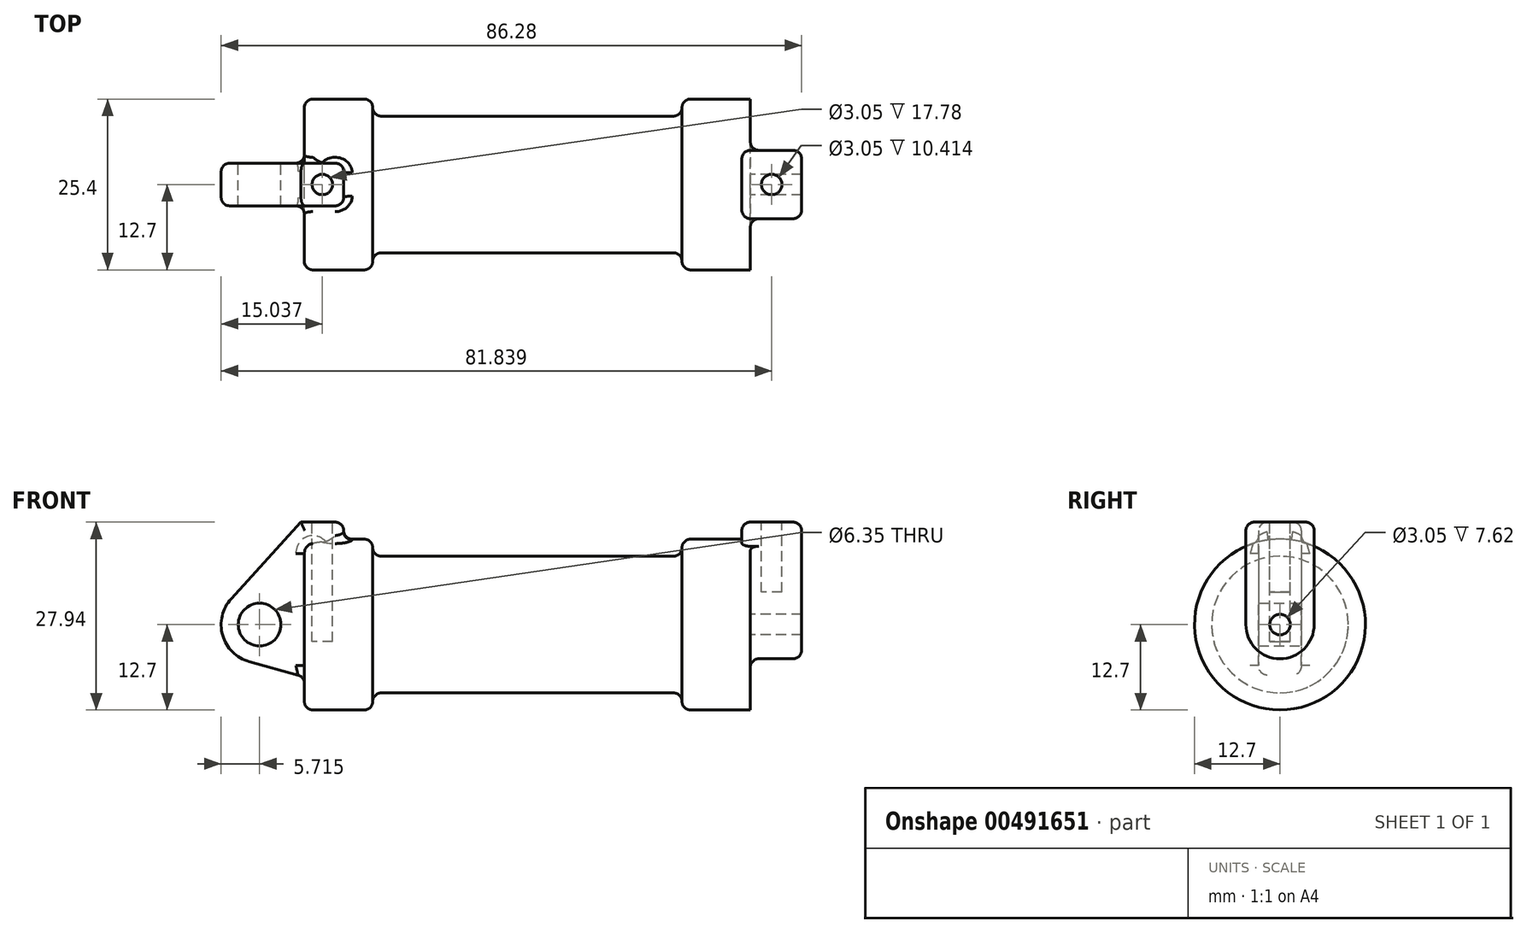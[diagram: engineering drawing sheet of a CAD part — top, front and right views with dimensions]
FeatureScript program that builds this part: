
annotation { "Feature Type Name" : "Feature", "Feature Type Description" : "" }
export const myFeature = defineFeature(function(context is Context, id is Id, definition is map)
    precondition{}
    {
        {
            var Q0;
            Q0=qCreatedBy(makeId("Front.planeOp"),FACE);
            var sketch = newSketch(context, id + "F0", { "sketchPlane" : qUnion([Q0])});
            skLineSegment(sketch, "E0", {"start": v(0, 0) * mm, "end": v(0, 12.7) * mm});
            skLineSegment(sketch, "E1", {"start": v(0, 12.7) * mm, "end": v(10.16, 12.7) * mm});
            skLineSegment(sketch, "E2", {"start": v(10.16, 12.7) * mm, "end": v(10.16, 10.16) * mm});
            skLineSegment(sketch, "E3", {"start": v(10.16, 10.16) * mm, "end": v(56.13, 10.16) * mm});
            skLineSegment(sketch, "E4", {"start": v(56.13, 10.16) * mm, "end": v(56.13, 12.7) * mm});
            skLineSegment(sketch, "E5", {"start": v(56.13, 12.7) * mm, "end": v(66.3, 12.7) * mm});
            skLineSegment(sketch, "E6", {"start": v(66.3, 12.7) * mm, "end": v(66.3, 0) * mm});
            skLineSegment(sketch, "E7", {"start": v(66.3, 0) * mm, "end": v(0, 0) * mm});
            skLineSegment(sketch, "E8", {"start": v(5.84, 15.24) * mm, "end": v(-0.5, 15.24) * mm});
            skLineSegment(sketch, "E9", {"start": v(-0.5, 15.24) * mm, "end": v(-10.88, 3.85) * mm});
            skLineSegment(sketch, "E10", {"start": v(0, 0) * mm, "end": v(-6.65, 0) * mm});
            skCircle(sketch, "E11", {"center": v(-6.65, 0) * mm, "radius": 5.72 * mm});
            skCircle(sketch, "E12", {"center": v(-6.65, 0) * mm, "radius": 3.18 * mm});
            skLineSegment(sketch, "E13", {"start": v(5.84, 15.24) * mm, "end": v(5.84, -9.4) * mm});
            skLineSegment(sketch, "E14", {"start": v(5.84, -9.4) * mm, "end": v(-8.18, -5.5) * mm});
            skSolve(sketch);
        }
        {
            var Q0;
            {var subQ0=sQuery(id+"F0.wireOp",EDGE,"E0");Q0=makeQuery(id+"F0.imprint","IMPRINT",FACE,{"disambiguationData":[TD([[makeQuery(id+"F0.imprint","IMPRINT",EDGE,{"derivedFrom":subQ0}),-1.0]])]});}
            var Q1;
            {var subQ0=sQuery(id+"F0.wireOp",EDGE,"E2");Q1=makeQuery(id+"F0.imprint","IMPRINT",FACE,{"disambiguationData":[TD([[makeQuery(id+"F0.imprint","IMPRINT",EDGE,{"derivedFrom":subQ0}),-1.0]])]});}
            var Q2;
            Q2=sQuery(id+"F0.wireOp",EDGE,"E7");
            revolve(context, id + "F1", {"entities" : qUnion([Q0, Q1]), "axis" : qUnion([Q2]), "revolveType" : RevolveType.FULL});
        }
        {
            var Q0;
            {var subQ5=sQuery(id+"F0.wireOp",EDGE,"E12");Q0=makeQuery(id+"F0.imprint","IMPRINT",FACE,{"disambiguationData":[TD([[makeQuery(id+"F0.imprint","IMPRINT",EDGE,{"derivedFrom":subQ5}),-1.0]])]});}
            var Q1;
            {var subQ1=sQuery(id+"F0.wireOp",EDGE,"E0");Q1=makeQuery(id+"F0.imprint","IMPRINT",FACE,{"disambiguationData":[TD([[makeQuery(id+"F0.imprint","IMPRINT",EDGE,{"derivedFrom":subQ1}),1.0]])]});}
            var Q2;
            {var subQ0=sQuery(id+"F0.wireOp",EDGE,"E0");Q2=makeQuery(id+"F0.imprint","IMPRINT",FACE,{"disambiguationData":[TD([[makeQuery(id+"F0.imprint","IMPRINT",EDGE,{"derivedFrom":subQ0}),-1.0]])]});}
            var Q3;
            {var subQ0=sQuery(id+"F0.wireOp",EDGE,"E14");Q3=makeQuery(id+"F0.imprint","IMPRINT",FACE,{"disambiguationData":[TD([[makeQuery(id+"F0.imprint","IMPRINT",EDGE,{"derivedFrom":subQ0}),-1.0]])]});}
            extrude(context, id + "F2", {"entities" : qUnion([Q0, Q1, Q2, Q3]), "operationType" : NewBodyOperationType.ADD, "endBound" : BoundingType.SYMMETRIC, "depth" : 6.35 * mm});
        }
        {
            var Q0;
            Q0=makeQuery(id+"F1.opRevolve","SWEPT_FACE",FACE,{"disambiguationData":[OSD([sQuery(id+"F0.wireOp",EDGE,"E6")])]});
            var sketch = newSketch(context, id + "F3", { "sketchPlane" : qUnion([Q0])});
            skCircle(sketch, "E15", {"center": v(0, 0) * mm, "radius": 5.08 * mm});
            skCircle(sketch, "E16", {"center": v(0, 0) * mm, "radius": 1.52 * mm});
            skLineSegment(sketch, "E17", {"start": v(-5.08, 15.24) * mm, "end": v(5.08, 15.24) * mm});
            skLineSegment(sketch, "E18", {"start": v(-5.08, 15.24) * mm, "end": v(-5.08, 0) * mm});
            skLineSegment(sketch, "E19", {"start": v(5.08, 15.24) * mm, "end": v(5.08, 0) * mm});
            skSolve(sketch);
        }
        {
            var Q0;
            {var subQ0=sQuery(id+"F3.wireOp",EDGE,"E17");Q0=makeQuery(id+"F3.imprint","IMPRINT",FACE,{"disambiguationData":[TD([[makeQuery(id+"F3.imprint","IMPRINT",EDGE,{"derivedFrom":subQ0}),-1.0]])]});}
            var Q1;
            {var subQ0=sQuery(id+"F3.wireOp",EDGE,"E18");var subQ1=sQuery(id+"F3.wireOp",EDGE,"E15");var subQ2=makeQuery(id+"F3.imprint","INTERSECT",VERTEX,{"derivedFrom":[subQ1,subQ0]});Q1=makeQuery(id+"F3.imprint","IMPRINT",FACE,{"disambiguationData":[TD([[makeQuery(id+"F3.imprint","IMPRINT",EDGE,{"disambiguationData":[TD([[subQ2,1.0]])],"derivedFrom":subQ1}),-1.0]])]});}
            var Q2;
            Q2=makeQuery(id+"F3.imprint","IMPRINT",FACE,{"disambiguationData":[TD([[makeQuery(id+"F3.imprint","IMPRINT",EDGE,{"derivedFrom":sQuery(id+"F3.wireOp",EDGE,"E16")}),-1.0]])]});
            extrude(context, id + "F4", {"entities" : qUnion([Q0, Q1, Q2]), "operationType" : NewBodyOperationType.ADD, "depth" : 7.62 * mm});
        }
        {
            var Q0;
            Q0=makeQuery(id+"F4.opExtrude","CAP_FACE",FACE,{"disambiguationData":[OSD([sQuery(id+"F3.wireOp",EDGE,"E15"),sQuery(id+"F3.wireOp",EDGE,"E16"),sQuery(id+"F3.wireOp",EDGE,"E17"),sQuery(id+"F3.wireOp",EDGE,"E18"),sQuery(id+"F3.wireOp",EDGE,"E19")])],"isStart":true});
            extrude(context, id + "F5", {"entities" : qUnion([Q0]), "operationType" : NewBodyOperationType.ADD, "depth" : 1.27 * mm});
        }
        {
            var Q0;
            Q0=makeQuery(id+"F4.boolean.opBoolean","SPLIT",FACE,{"disambiguationData":[TD([makeQuery(id+"F4.opExtrude","SWEPT_FACE",FACE,{"disambiguationData":[OSD([sQuery(id+"F3.wireOp",EDGE,"E16")])]})])],"derivedFrom":makeQuery(id+"F1.opRevolve","SWEPT_FACE",FACE,{"disambiguationData":[OSD([sQuery(id+"F0.wireOp",EDGE,"E6")])]})});
            var Q1;
            Q1=makeQuery(id+"F1.opRevolve","SWEPT_FACE",FACE,{"disambiguationData":[OSD([sQuery(id+"F0.wireOp",EDGE,"E2")])]});
            extrude(context, id + "F6", {"entities" : qUnion([Q0]), "operationType" : NewBodyOperationType.ADD, "endBound" : BoundingType.UP_TO_SURFACE, "oppositeDirection" : true, "endBoundEntityFace" : qUnion([Q1]), "depth" : 25.4 * mm});
        }
        {
            var Q0;
            Q0=makeQuery(id+"F2.opExtrude","SWEPT_FACE",FACE,{"disambiguationData":[OSD([sQuery(id+"F0.wireOp",EDGE,"E8")])]});
            var sketch = newSketch(context, id + "F7", { "sketchPlane" : qUnion([Q0])});
            skLineSegment(sketch, "E20", {"start": v(2.67, 3.18) * mm, "end": v(2.67, -3.18) * mm, "construction": true});
            skCircle(sketch, "E21", {"center": v(2.67, 0) * mm, "radius": 1.52 * mm});
            skSolve(sketch);
        }
        {
            var Q0;
            {var subQ0=sQuery(id+"F3.wireOp",EDGE,"E17");Q0=makeQuery(id+"F5.boolean.opBoolean","MERGE",FACE,{"derivedFrom":[makeQuery(id+"F4.opExtrude","SWEPT_FACE",FACE,{"disambiguationData":[OSD([subQ0])]}),makeQuery(id+"F5.opExtrude","SWEPT_FACE",FACE,{"disambiguationData":[OSD([subQ0])]})]});}
            var sketch = newSketch(context, id + "F8", { "sketchPlane" : qUnion([Q0])});
            skLineSegment(sketch, "E22", {"start": v(65.02, 0) * mm, "end": v(73.91, 0) * mm, "construction": true});
            skCircle(sketch, "E23", {"center": v(69.47, 0) * mm, "radius": 1.52 * mm});
            skSolve(sketch);
        }
        {
            var Q0;
            Q0=makeQuery(id+"F7.imprint","IMPRINT",FACE,{"disambiguationData":[TD([[makeQuery(id+"F7.imprint","IMPRINT",EDGE,{"derivedFrom":sQuery(id+"F7.wireOp",EDGE,"E21")}),1.0]])]});
            extrude(context, id + "F9", {"entities" : qUnion([Q0]), "operationType" : NewBodyOperationType.REMOVE, "oppositeDirection" : true, "depth" : 17.78 * mm});
        }
        {
            var Q0;
            Q0=makeQuery(id+"F8.imprint","IMPRINT",FACE,{"disambiguationData":[TD([[makeQuery(id+"F8.imprint","IMPRINT",EDGE,{"derivedFrom":sQuery(id+"F8.wireOp",EDGE,"E23")}),1.0]])]});
            extrude(context, id + "F10", {"entities" : qUnion([Q0]), "operationType" : NewBodyOperationType.REMOVE, "oppositeDirection" : true, "depth" : 10.4 * mm});
        }
        {
            var Q0;
            Q0=makeQuery(id+"F2.boolean.opBoolean","INTERSECT",EDGE,{"derivedFrom":[makeQuery(id+"F1.opRevolve","SWEPT_FACE",FACE,{"disambiguationData":[OSD([sQuery(id+"F0.wireOp",EDGE,"E1")])]}),makeQuery(id+"F2.opExtrude","SWEPT_FACE",FACE,{"disambiguationData":[OSD([sQuery(id+"F0.wireOp",EDGE,"E13")])]})]});
            var Q1;
            Q1=makeQuery(id+"F2.opExtrude","CAP_EDGE",EDGE,{"disambiguationData":[OSD([sQuery(id+"F0.wireOp",EDGE,"E13")])],"isStart":false});
            var Q2;
            Q2=makeQuery(id+"F2.opExtrude","SWEPT_EDGE",EDGE,{"disambiguationData":[OSD([sQuery(id+"F0.wireOp",EDGE,"E8"),sQuery(id+"F0.wireOp",EDGE,"E13")])]});
            var Q3;
            Q3=makeQuery(id+"F2.opExtrude","CAP_EDGE",EDGE,{"disambiguationData":[OSD([sQuery(id+"F0.wireOp",EDGE,"E13")])],"isStart":true});
            var Q4;
            Q4=makeQuery(id+"F2.opExtrude","CAP_EDGE",EDGE,{"disambiguationData":[OSD([sQuery(id+"F0.wireOp",EDGE,"E8")])],"isStart":false});
            var Q5;
            Q5=makeQuery(id+"F2.opExtrude","CAP_EDGE",EDGE,{"disambiguationData":[OSD([sQuery(id+"F0.wireOp",EDGE,"E9")])],"isStart":false});
            fillet(context, id + "F11", {"entities" : qUnion([Q0, Q1, Q2, Q3, Q4, Q5]), "radius" : 1.27 * mm, "tangentPropagation" : true, "allowEdgeOverflow" : false});
        }
        {
            var Q0;
            Q0=makeQuery(id+"F2.boolean.opBoolean","INTERSECT",EDGE,{"derivedFrom":[makeQuery(id+"F1.opRevolve","SWEPT_FACE",FACE,{"disambiguationData":[OSD([sQuery(id+"F0.wireOp",EDGE,"E0")])]}),makeQuery(id+"F2.opExtrude","CAP_FACE",FACE,{"disambiguationData":[OSD([sQuery(id+"F0.wireOp",EDGE,"E8"),sQuery(id+"F0.wireOp",EDGE,"E9"),sQuery(id+"F0.wireOp",EDGE,"E11"),sQuery(id+"F0.wireOp",EDGE,"E12"),sQuery(id+"F0.wireOp",EDGE,"E13"),sQuery(id+"F0.wireOp",EDGE,"E14")])],"isStart":true})]});
            var Q1;
            Q1=makeQuery(id+"F1.opRevolve","SWEPT_EDGE",EDGE,{"disambiguationData":[OSD([sQuery(id+"F0.wireOp",EDGE,"E0"),sQuery(id+"F0.wireOp",EDGE,"E1")])]});
            var Q2;
            Q2=makeQuery(id+"F1.opRevolve","SWEPT_EDGE",EDGE,{"disambiguationData":[OSD([sQuery(id+"F0.wireOp",EDGE,"E1"),sQuery(id+"F0.wireOp",EDGE,"E2")])]});
            var Q3;
            Q3=makeQuery(id+"F1.opRevolve","SWEPT_EDGE",EDGE,{"disambiguationData":[OSD([sQuery(id+"F0.wireOp",EDGE,"E3"),sQuery(id+"F0.wireOp",EDGE,"E4")])]});
            var Q4;
            Q4=makeQuery(id+"F1.opRevolve","SWEPT_EDGE",EDGE,{"disambiguationData":[OSD([sQuery(id+"F0.wireOp",EDGE,"E4"),sQuery(id+"F0.wireOp",EDGE,"E5")])]});
            var Q5;
            Q5=makeQuery(id+"F1.opRevolve","SWEPT_EDGE",EDGE,{"disambiguationData":[OSD([sQuery(id+"F0.wireOp",EDGE,"E2"),sQuery(id+"F0.wireOp",EDGE,"E3")])]});
            fillet(context, id + "F12", {"entities" : qUnion([Q0, Q1, Q2, Q3, Q4, Q5]), "radius" : 1.27 * mm, "tangentPropagation" : true, "allowEdgeOverflow" : false});
        }
        {
            var Q0;
            {var subQ0=sQuery(id+"F3.wireOp",EDGE,"E18");var subQ1=sQuery(id+"F3.wireOp",EDGE,"E17");Q0=makeQuery(id+"F5.boolean.opBoolean","MERGE",EDGE,{"derivedFrom":[makeQuery(id+"F4.opExtrude","SWEPT_EDGE",EDGE,{"disambiguationData":[OSD([subQ1,subQ0])]}),makeQuery(id+"F5.opExtrude","SWEPT_EDGE",EDGE,{"disambiguationData":[OSD([subQ1,subQ0])]})]});}
            var Q1;
            Q1=makeQuery(id+"F4.opExtrude","CAP_EDGE",EDGE,{"disambiguationData":[OSD([sQuery(id+"F3.wireOp",EDGE,"E17")])],"isStart":false});
            var Q2;
            {var subQ0=sQuery(id+"F3.wireOp",EDGE,"E19");var subQ1=sQuery(id+"F3.wireOp",EDGE,"E17");Q2=makeQuery(id+"F5.boolean.opBoolean","MERGE",EDGE,{"derivedFrom":[makeQuery(id+"F4.opExtrude","SWEPT_EDGE",EDGE,{"disambiguationData":[OSD([subQ1,subQ0])]}),makeQuery(id+"F5.opExtrude","SWEPT_EDGE",EDGE,{"disambiguationData":[OSD([subQ1,subQ0])]})]});}
            var Q3;
            Q3=makeQuery(id+"F4.opExtrude","CAP_EDGE",EDGE,{"disambiguationData":[OSD([sQuery(id+"F3.wireOp",EDGE,"E18")])],"isStart":false});
            var Q4;
            Q4=makeQuery(id+"F5.opExtrude","CAP_EDGE",EDGE,{"disambiguationData":[OSD([sQuery(id+"F3.wireOp",EDGE,"E18")])],"isStart":false});
            var Q5;
            Q5=makeQuery(id+"F4.opExtrude","SWEPT_EDGE",EDGE,{"disambiguationData":[OSD([sQuery(id+"F3.wireOp",EDGE,"E15"),sQuery(id+"F3.wireOp",EDGE,"E18")])]});
            var Q6;
            Q6=makeQuery(id+"F4.opExtrude","CAP_EDGE",EDGE,{"disambiguationData":[OSD([sQuery(id+"F3.wireOp",EDGE,"E15")])],"isStart":false});
            var Q7;
            Q7=makeQuery(id+"F4.opExtrude","CAP_EDGE",EDGE,{"disambiguationData":[OSD([sQuery(id+"F3.wireOp",EDGE,"E15")])],"isStart":true});
            var Q8;
            Q8=makeQuery(id+"F4.opExtrude","CAP_EDGE",EDGE,{"disambiguationData":[OSD([sQuery(id+"F3.wireOp",EDGE,"E19")])],"isStart":false});
            var Q9;
            {var subQ0=sQuery(id+"F3.wireOp",EDGE,"E19");Q9=makeQuery(id+"F4.boolean.opBoolean","SPLIT",EDGE,{"disambiguationData":[topologyDisambiguationEdgeConnected([makeQuery(id+"F1.opRevolve","SWEPT_FACE",FACE,{"disambiguationData":[OSD([sQuery(id+"F0.wireOp",EDGE,"E6")])]})])],"derivedFrom":makeQuery(id+"F4.opExtrude","CAP_EDGE",EDGE,{"disambiguationData":[OSD([subQ0])],"isStart":true})});}
            var Q10;
            Q10=makeQuery(id+"F5.opExtrude","CAP_EDGE",EDGE,{"disambiguationData":[OSD([sQuery(id+"F3.wireOp",EDGE,"E19")])],"isStart":false});
            var Q11;
            Q11=makeQuery(id+"F5.opExtrude","CAP_EDGE",EDGE,{"disambiguationData":[OSD([sQuery(id+"F3.wireOp",EDGE,"E17")])],"isStart":false});
            fillet(context, id + "F13", {"entities" : qUnion([Q0, Q1, Q2, Q3, Q4, Q5, Q6, Q7, Q8, Q9, Q10, Q11]), "radius" : 1.27 * mm, "tangentPropagation" : true, "allowEdgeOverflow" : false});
        }
        {
            var Q0;
            Q0=makeQuery(id+"F5.opExtrude","CAP_EDGE",EDGE,{"disambiguationData":[OSD([sQuery(id+"F0.wireOp",EDGE,"E5"),sQuery(id+"F0.wireOp",EDGE,"E6")])],"isStart":false});
            var Q1;
            Q1=makeQuery(id+"F2.opExtrude","CAP_EDGE",EDGE,{"disambiguationData":[OSD([sQuery(id+"F0.wireOp",EDGE,"E9")])],"isStart":true});
            var Q2;
            Q2=makeQuery(id+"F2.opExtrude","CAP_EDGE",EDGE,{"disambiguationData":[OSD([sQuery(id+"F0.wireOp",EDGE,"E8")])],"isStart":true});
            var Q3;
            Q3=makeQuery(id+"F2.boolean.opBoolean","INTERSECT",EDGE,{"derivedFrom":[makeQuery(id+"F1.opRevolve","SWEPT_FACE",FACE,{"disambiguationData":[OSD([sQuery(id+"F0.wireOp",EDGE,"E0")])]}),makeQuery(id+"F2.opExtrude","CAP_FACE",FACE,{"disambiguationData":[OSD([sQuery(id+"F0.wireOp",EDGE,"E8"),sQuery(id+"F0.wireOp",EDGE,"E9"),sQuery(id+"F0.wireOp",EDGE,"E11"),sQuery(id+"F0.wireOp",EDGE,"E12"),sQuery(id+"F0.wireOp",EDGE,"E13"),sQuery(id+"F0.wireOp",EDGE,"E14")])],"isStart":false})]});
            fillet(context, id + "F14", {"entities" : qUnion([Q0, Q1, Q2, Q3]), "radius" : 1.27 * mm, "tangentPropagation" : true, "allowEdgeOverflow" : false});
        }
    });
